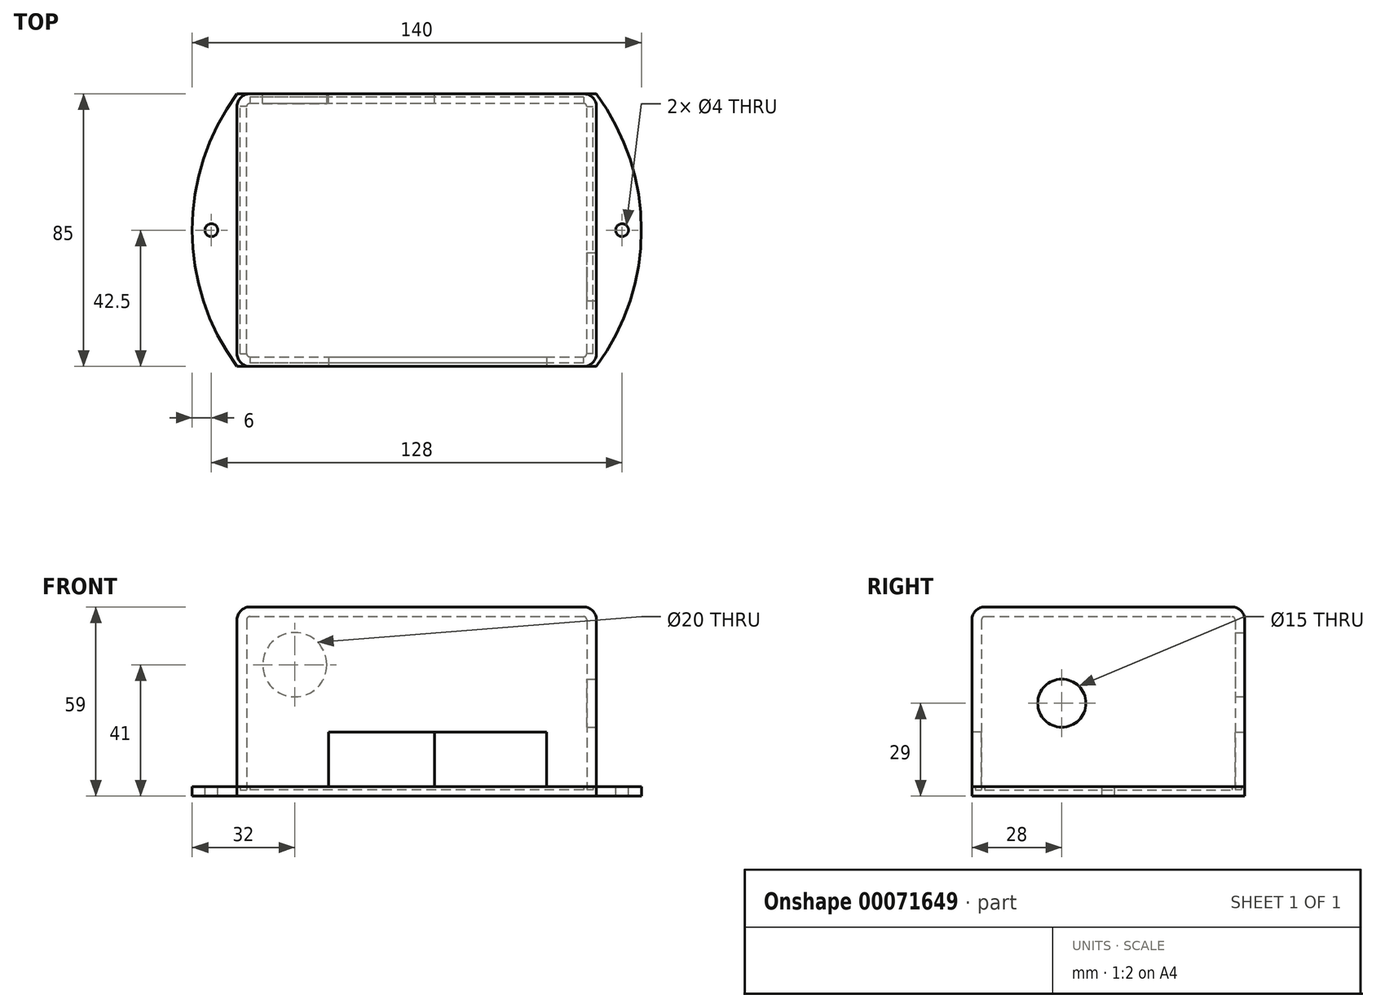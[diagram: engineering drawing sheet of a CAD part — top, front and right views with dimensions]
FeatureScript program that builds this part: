
annotation { "Feature Type Name" : "Feature", "Feature Type Description" : "" }
export const myFeature = defineFeature(function(context is Context, id is Id, definition is map)
    precondition{}
    {
        {
            var Q0;
            Q0=qCreatedBy(makeId("Top.planeOp"),FACE);
            var sketch = newSketch(context, id + "F0", { "sketchPlane" : qUnion([Q0])});
            skLineSegment(sketch, "E0.rect.bottom", {"start": v(56, 42.5) * mm, "end": v(-56, 42.5) * mm});
            skLineSegment(sketch, "E0.rect.top", {"start": v(56, -42.5) * mm, "end": v(-56, -42.5) * mm});
            skLineSegment(sketch, "E0.rect.left", {"start": v(56, 42.5) * mm, "end": v(56, -42.5) * mm});
            skLineSegment(sketch, "E0.rect.right", {"start": v(-56, 42.5) * mm, "end": v(-56, -42.5) * mm});
            skPoint(sketch, "E0.rect.middle", {"position": v(0, 0) * mm});
            skSolve(sketch);
        }
        {
            var Q0;
            Q0 = qSketchRegion(id + "F0", true);
            extrude(context, id + "F1", {"entities" : qUnion([Q0]), "depth" : 57 * mm});
        }
        {
            var Q0;
            Q0=makeQuery(id+"F1.opExtrude","SWEPT_EDGE",EDGE,{"disambiguationData":[OSD([sQuery(id+"F0.wireOp",EDGE,"E0.rect.top"),sQuery(id+"F0.wireOp",EDGE,"E0.rect.left")])]});
            var Q1;
            Q1=makeQuery(id+"F1.opExtrude","SWEPT_EDGE",EDGE,{"disambiguationData":[OSD([sQuery(id+"F0.wireOp",EDGE,"E0.rect.top"),sQuery(id+"F0.wireOp",EDGE,"E0.rect.right")])]});
            var Q2;
            Q2=makeQuery(id+"F1.opExtrude","CAP_EDGE",EDGE,{"disambiguationData":[OSD([sQuery(id+"F0.wireOp",EDGE,"E0.rect.top")])],"isStart":false});
            var Q3;
            Q3=makeQuery(id+"F1.opExtrude","CAP_EDGE",EDGE,{"disambiguationData":[OSD([sQuery(id+"F0.wireOp",EDGE,"E0.rect.right")])],"isStart":false});
            var Q4;
            Q4=makeQuery(id+"F1.opExtrude","CAP_EDGE",EDGE,{"disambiguationData":[OSD([sQuery(id+"F0.wireOp",EDGE,"E0.rect.left")])],"isStart":false});
            var Q5;
            Q5=makeQuery(id+"F1.opExtrude","SWEPT_EDGE",EDGE,{"disambiguationData":[OSD([sQuery(id+"F0.wireOp",EDGE,"E0.rect.bottom"),sQuery(id+"F0.wireOp",EDGE,"E0.rect.left")])]});
            var Q6;
            Q6=makeQuery(id+"F1.opExtrude","CAP_EDGE",EDGE,{"disambiguationData":[OSD([sQuery(id+"F0.wireOp",EDGE,"E0.rect.bottom")])],"isStart":false});
            var Q7;
            Q7=makeQuery(id+"F1.opExtrude","SWEPT_EDGE",EDGE,{"disambiguationData":[OSD([sQuery(id+"F0.wireOp",EDGE,"E0.rect.bottom"),sQuery(id+"F0.wireOp",EDGE,"E0.rect.right")])]});
            fillet(context, id + "F2", {"entities" : qUnion([Q0, Q1, Q2, Q3, Q4, Q5, Q6, Q7]), "radius" : 4 * mm, "tangentPropagation" : true, "allowEdgeOverflow" : false});
        }
        {
            var Q0;
            Q0=makeQuery(id+"F1.opExtrude","CAP_FACE",FACE,{"disambiguationData":[OSD([sQuery(id+"F0.wireOp",EDGE,"E0.rect.bottom"),sQuery(id+"F0.wireOp",EDGE,"E0.rect.top"),sQuery(id+"F0.wireOp",EDGE,"E0.rect.left"),sQuery(id+"F0.wireOp",EDGE,"E0.rect.right")])],"isStart":true});
            shell(context, id + "F3", {"entities" : qUnion([Q0]), "thickness" : 3 * mm});
        }
        {
            var Q0;
            Q0=makeQuery(id+"F1.opExtrude","CAP_FACE",FACE,{"disambiguationData":[OSD([sQuery(id+"F0.wireOp",EDGE,"E0.rect.bottom"),sQuery(id+"F0.wireOp",EDGE,"E0.rect.top"),sQuery(id+"F0.wireOp",EDGE,"E0.rect.left"),sQuery(id+"F0.wireOp",EDGE,"E0.rect.right")])],"isStart":true});
            var sketch = newSketch(context, id + "F4", { "sketchPlane" : qUnion([Q0])});
            skLineSegment(sketch, "E1.rect.top", {"start": v(52, -41.5) * mm, "end": v(-52, -41.5) * mm});
            skLineSegment(sketch, "E1.rect.right", {"start": v(-55, 38.5) * mm, "end": v(-55, -38.5) * mm});
            skPoint(sketch, "E1.rect.middle", {"position": v(0, 0) * mm});
            skLineSegment(sketch, "E2.rect.bottom", {"start": v(64.66, 50.6) * mm, "end": v(-64.66, 50.6) * mm});
            skLineSegment(sketch, "E2.rect.top", {"start": v(64.66, -50.6) * mm, "end": v(-64.66, -50.6) * mm});
            skLineSegment(sketch, "E2.rect.left", {"start": v(64.66, 50.6) * mm, "end": v(64.66, -50.6) * mm});
            skLineSegment(sketch, "E2.rect.right", {"start": v(-64.66, 50.6) * mm, "end": v(-64.66, -50.6) * mm});
            skLineSegment(sketch, "E3", {"start": v(-55, 38.5) * mm, "end": v(-53, 38.5) * mm});
            skLineSegment(sketch, "E4", {"start": v(-53, 38.5) * mm, "end": v(-52, 38.5) * mm});
            skLineSegment(sketch, "E5", {"start": v(-52, 38.5) * mm, "end": v(-52, 41.5) * mm});
            skLineSegment(sketch, "E6", {"start": v(-52, -41.5) * mm, "end": v(-52, -38.5) * mm});
            skLineSegment(sketch, "E7", {"start": v(-52, -38.5) * mm, "end": v(-55, -38.5) * mm});
            skLineSegment(sketch, "E8", {"start": v(52, -41.5) * mm, "end": v(52, -38.5) * mm});
            skLineSegment(sketch, "E9", {"start": v(52, -38.5) * mm, "end": v(55, -38.5) * mm});
            skLineSegment(sketch, "E10.top", {"start": v(55, 38.5) * mm, "end": v(52, 38.5) * mm});
            skLineSegment(sketch, "E10.right", {"start": v(52, 41.5) * mm, "end": v(52, 38.5) * mm});
            skLineSegment(sketch, "E11.trimOffspring", {"start": v(55, 38.5) * mm, "end": v(55, -38.5) * mm});
            skLineSegment(sketch, "E12.trimOffspring", {"start": v(52, 41.5) * mm, "end": v(-52, 41.5) * mm});
            skSolve(sketch);
        }
        {
            var Q0;
            Q0 = qSketchRegion(id + "F4", true);
            extrude(context, id + "F5", {"entities" : qUnion([Q0]), "operationType" : NewBodyOperationType.REMOVE, "oppositeDirection" : true, "depth" : 1 * mm});
        }
        {
            var Q0;
            Q0=makeQuery(id+"F5.boolean.opBoolean","COPY",FACE,{"derivedFrom":makeQuery(id+"F5.opExtrude","CAP_FACE",FACE,{"disambiguationData":[OSD([sQuery(id+"F4.wireOp",EDGE,"E1.rect.top"),sQuery(id+"F4.wireOp",EDGE,"E1.rect.right"),sQuery(id+"F4.wireOp",EDGE,"E2.rect.bottom"),sQuery(id+"F4.wireOp",EDGE,"E2.rect.top"),sQuery(id+"F4.wireOp",EDGE,"E2.rect.left"),sQuery(id+"F4.wireOp",EDGE,"E2.rect.right"),sQuery(id+"F4.wireOp",EDGE,"E3"),sQuery(id+"F4.wireOp",EDGE,"E4"),sQuery(id+"F4.wireOp",EDGE,"E5"),sQuery(id+"F4.wireOp",EDGE,"E6"),sQuery(id+"F4.wireOp",EDGE,"E7"),sQuery(id+"F4.wireOp",EDGE,"E8"),sQuery(id+"F4.wireOp",EDGE,"E9"),sQuery(id+"F4.wireOp",EDGE,"E10.top"),sQuery(id+"F4.wireOp",EDGE,"E10.right"),sQuery(id+"F4.wireOp",EDGE,"E11.trimOffspring"),sQuery(id+"F4.wireOp",EDGE,"E12.trimOffspring")])],"isStart":false})});
            var sketch = newSketch(context, id + "F6", { "sketchPlane" : qUnion([Q0])});
            skLineSegment(sketch, "E13.rect.bottom", {"start": v(56, 42.5) * mm, "end": v(-56, 42.5) * mm});
            skLineSegment(sketch, "E13.rect.top", {"start": v(56, -42.5) * mm, "end": v(-56, -42.5) * mm});
            skLineSegment(sketch, "E13.rect.left", {"start": v(56, 42.5) * mm, "end": v(56, -42.5) * mm});
            skLineSegment(sketch, "E13.rect.right", {"start": v(-56, 42.5) * mm, "end": v(-56, -42.5) * mm});
            skPoint(sketch, "E13.rect.middle", {"position": v(0, 0) * mm});
            skLineSegment(sketch, "E14", {"start": v(-70, 0) * mm, "end": v(70, 0) * mm, "construction": true});
            skArc(sketch, "E15", {"start": v(-56, 42.5) * mm, "mid": v(-70, 0) * mm, "end": v(-56, -42.5) * mm});
            skArc(sketch, "E16", {"start": v(56, -42.5) * mm, "mid": v(70, 0) * mm, "end": v(56, 42.5) * mm});
            skCircle(sketch, "E17", {"center": v(-64, 0) * mm, "radius": 2 * mm});
            skCircle(sketch, "E18", {"center": v(64, 0) * mm, "radius": 2 * mm});
            skSolve(sketch);
        }
        {
            var Q0;
            Q0 = qSketchRegion(id + "F6", true);
            extrude(context, id + "F7", {"entities" : qUnion([Q0]), "depth" : 3 * mm});
        }
        {
            var Q0;
            Q0=makeQuery(id+"F1.opExtrude","SWEPT_FACE",FACE,{"disambiguationData":[OSD([sQuery(id+"F0.wireOp",EDGE,"E0.rect.top")])]});
            var sketch = newSketch(context, id + "F8", { "sketchPlane" : qUnion([Q0])});
            skLineSegment(sketch, "E19.bottom", {"start": v(40.5, 1) * mm, "end": v(-27.5, 1) * mm});
            skLineSegment(sketch, "E19.top", {"start": v(40.5, 18) * mm, "end": v(-27.5, 18) * mm});
            skLineSegment(sketch, "E19.left", {"start": v(40.5, 1) * mm, "end": v(40.5, 18) * mm});
            skLineSegment(sketch, "E19.right", {"start": v(-27.5, 1) * mm, "end": v(-27.5, 18) * mm});
            skSolve(sketch);
        }
        {
            var Q0;
            Q0 = qSketchRegion(id + "F8", true);
            extrude(context, id + "F9", {"entities" : qUnion([Q0]), "operationType" : NewBodyOperationType.REMOVE, "oppositeDirection" : true, "depth" : 3 * mm});
        }
        {
            var Q0;
            Q0=makeQuery(id+"F1.opExtrude","SWEPT_FACE",FACE,{"disambiguationData":[OSD([sQuery(id+"F0.wireOp",EDGE,"E0.rect.bottom")])]});
            var sketch = newSketch(context, id + "F10", { "sketchPlane" : qUnion([Q0])});
            skLineSegment(sketch, "E20.bottom", {"start": v(-5.5, 1) * mm, "end": v(27.5, 1) * mm});
            skLineSegment(sketch, "E20.top", {"start": v(-5.5, 18) * mm, "end": v(27.5, 18) * mm});
            skLineSegment(sketch, "E20.left", {"start": v(-5.5, 1) * mm, "end": v(-5.5, 18) * mm});
            skLineSegment(sketch, "E20.right", {"start": v(27.5, 1) * mm, "end": v(27.5, 18) * mm});
            skSolve(sketch);
        }
        {
            var Q0;
            Q0 = qSketchRegion(id + "F10", true);
            extrude(context, id + "F11", {"entities" : qUnion([Q0]), "operationType" : NewBodyOperationType.REMOVE, "oppositeDirection" : true, "depth" : 3 * mm});
        }
        {
            var Q0;
            Q0=makeQuery(id+"F1.opExtrude","SWEPT_FACE",FACE,{"disambiguationData":[OSD([sQuery(id+"F0.wireOp",EDGE,"E0.rect.bottom")])]});
            var sketch = newSketch(context, id + "F12", { "sketchPlane" : qUnion([Q0])});
            skCircle(sketch, "E21", {"center": v(38, 39) * mm, "radius": 10 * mm});
            skSolve(sketch);
        }
        {
            var Q0;
            Q0 = qSketchRegion(id + "F12", true);
            extrude(context, id + "F13", {"entities" : qUnion([Q0]), "operationType" : NewBodyOperationType.REMOVE, "oppositeDirection" : true, "depth" : 3 * mm});
        }
        {
            var Q0;
            Q0=makeQuery(id+"F1.opExtrude","SWEPT_FACE",FACE,{"disambiguationData":[OSD([sQuery(id+"F0.wireOp",EDGE,"E0.rect.left")])]});
            var sketch = newSketch(context, id + "F14", { "sketchPlane" : qUnion([Q0])});
            skCircle(sketch, "E22", {"center": v(-14.5, 27) * mm, "radius": 7.5 * mm});
            skPoint(sketch, "E22.centerSnap0", {"position": v(-38.5, 27) * mm});
            skSolve(sketch);
        }
        {
            var Q0;
            Q0 = qSketchRegion(id + "F14", true);
            extrude(context, id + "F15", {"entities" : qUnion([Q0]), "operationType" : NewBodyOperationType.REMOVE, "oppositeDirection" : true, "depth" : 3 * mm});
        }
    });
